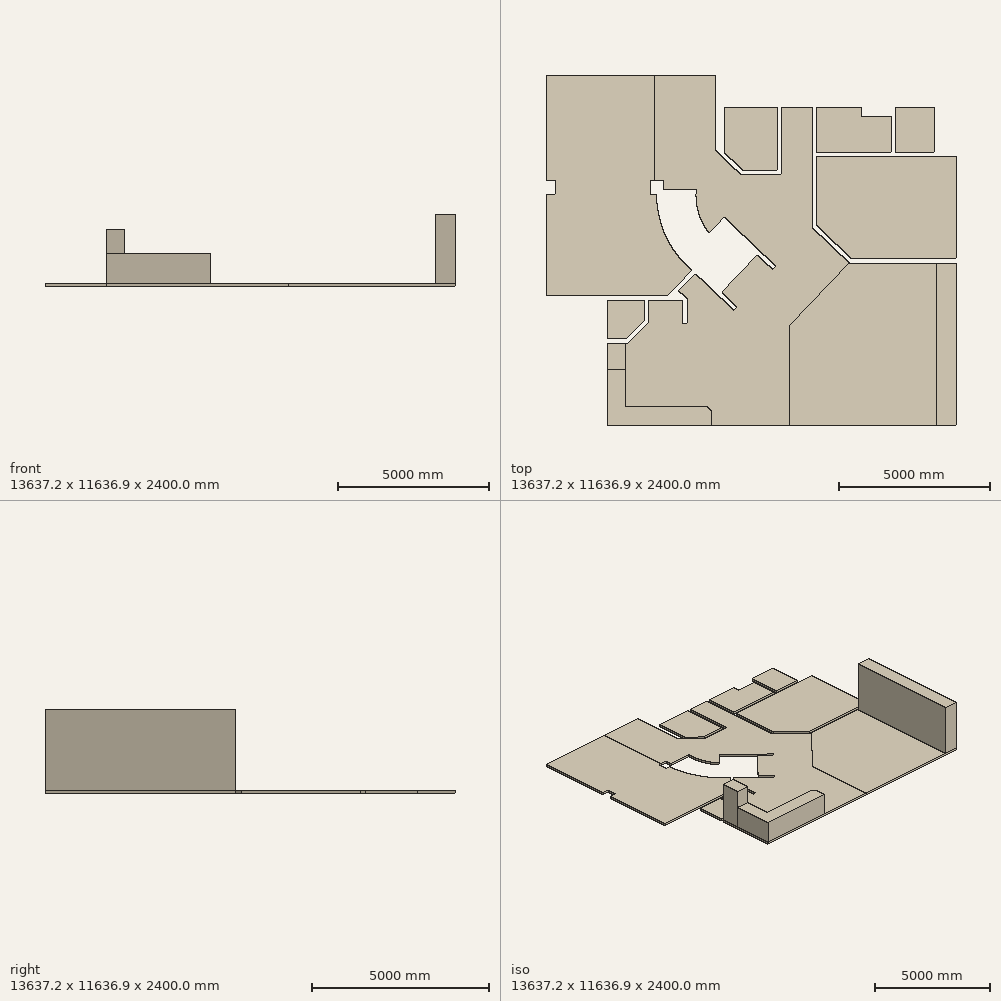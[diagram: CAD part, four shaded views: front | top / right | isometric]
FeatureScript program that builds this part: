
annotation { "Feature Type Name" : "Feature", "Feature Type Description" : "" }
export const myFeature = defineFeature(function(context is Context, id is Id, definition is map)
    precondition{}
    {
        {
            var Q0;
            Q0=qCreatedBy(makeId("Top.planeOp"),FACE);
            var sketch = newSketch(context, id + "F0", { "sketchPlane" : qUnion([Q0])});
            skLineSegment(sketch, "E0", {"start": v(-2600, 0) * mm, "end": v(0, 0) * mm});
            skLineSegment(sketch, "E1", {"start": v(0, 0) * mm, "end": v(0, 3300) * mm});
            skLineSegment(sketch, "E2", {"start": v(770, 6571.43) * mm, "end": v(770, 10720) * mm});
            skLineSegment(sketch, "E3", {"start": v(770, 10720) * mm, "end": v(-230, 10720) * mm});
            skLineSegment(sketch, "E4", {"start": v(-250, 10570) * mm, "end": v(-250, 8330) * mm});
            skLineSegment(sketch, "E5", {"start": v(-250, 8330) * mm, "end": v(-1600, 8330) * mm});
            skLineSegment(sketch, "E6", {"start": v(-1600, 8330) * mm, "end": v(-2447.24, 9136.9) * mm});
            skLineSegment(sketch, "E7", {"start": v(-2447.24, 9136.9) * mm, "end": v(-2447.24, 11636.9) * mm});
            skLineSegment(sketch, "E8", {"start": v(-2447.24, 11636.9) * mm, "end": v(-4497.24, 11636.9) * mm});
            skLineSegment(sketch, "E9", {"start": v(-4497.24, 11636.9) * mm, "end": v(-4497.24, 8136.9) * mm});
            skLineSegment(sketch, "E10", {"start": v(-4497.24, 8136.9) * mm, "end": v(-4197.24, 8136.9) * mm});
            skLineSegment(sketch, "E11", {"start": v(-4197.24, 8136.9) * mm, "end": v(-4197.24, 7836.9) * mm});
            skLineSegment(sketch, "E12", {"start": v(-4197.24, 7836.9) * mm, "end": v(-3097.24, 7836.9) * mm});
            skLineSegment(sketch, "E13", {"start": v(-4830, 3450) * mm, "end": v(-4830, 4170) * mm});
            skLineSegment(sketch, "E14", {"start": v(-4830, 4170) * mm, "end": v(-5900, 4170) * mm});
            skLineSegment(sketch, "E15", {"start": v(-2600, 0) * mm, "end": v(-2600, 488.01) * mm});
            skLineSegment(sketch, "E16", {"start": v(-2600, 488.01) * mm, "end": v(-2730, 640) * mm});
            skLineSegment(sketch, "E17", {"start": v(-2730, 640) * mm, "end": v(-5450, 640) * mm});
            skLineSegment(sketch, "E18", {"start": v(-5450, 640) * mm, "end": v(-5450, 2730) * mm});
            skLineSegment(sketch, "E19", {"start": v(-5400, 2880) * mm, "end": v(-4830, 3450) * mm});
            skLineSegment(sketch, "E20", {"start": v(-4680, 4170) * mm, "end": v(-4680, 3400) * mm});
            skLineSegment(sketch, "E21", {"start": v(-4921.42, 3358.58) * mm, "end": v(-4821.42, 3258.58) * mm});
            skLineSegment(sketch, "E22", {"start": v(-4680, 4170) * mm, "end": v(-3540, 4170) * mm});
            skLineSegment(sketch, "E23", {"start": v(-3540, 4170) * mm, "end": v(-3540, 3400) * mm});
            skLineSegment(sketch, "E24", {"start": v(-3390, 3400) * mm, "end": v(-3540, 3400) * mm});
            skLineSegment(sketch, "E25", {"start": v(-3390, 3400) * mm, "end": v(-3390, 4200) * mm});
            skLineSegment(sketch, "E26", {"start": v(-3125.52, 5049.31) * mm, "end": v(-1843.8, 3828.62) * mm});
            skLineSegment(sketch, "E27", {"start": v(-1843.8, 3828.62) * mm, "end": v(-1740.34, 3937.24) * mm});
            skLineSegment(sketch, "E28", {"start": v(-1740.34, 3937.24) * mm, "end": v(-2247.24, 4420) * mm});
            skLineSegment(sketch, "E29", {"start": v(-2247.24, 4420) * mm, "end": v(-1058.97, 5667.69) * mm});
            skLineSegment(sketch, "E30", {"start": v(-1058.97, 5667.69) * mm, "end": v(-552.07, 5184.93) * mm});
            skLineSegment(sketch, "E31", {"start": v(-552.07, 5184.93) * mm, "end": v(-448.62, 5293.55) * mm});
            skLineSegment(sketch, "E32", {"start": v(-448.62, 5293.55) * mm, "end": v(-2157.59, 6921.14) * mm});
            skLineSegment(sketch, "E33", {"start": v(-2157.59, 6921.14) * mm, "end": v(-2663.1, 6390.34) * mm});
            skArc(sketch, "E34", {"start": v(-3097.24, 7836.9) * mm, "mid": v(-3021.97, 7071.07) * mm, "end": v(-2663.1, 6390.34) * mm});
            skLineSegment(sketch, "E35", {"start": v(0, 0) * mm, "end": v(4900, 0) * mm});
            skLineSegment(sketch, "E36", {"start": v(4900, 0) * mm, "end": v(4900, 5400) * mm});
            skLineSegment(sketch, "E37", {"start": v(4900, 5400) * mm, "end": v(2000, 5400) * mm});
            skLineSegment(sketch, "E38", {"start": v(0, 3300) * mm, "end": v(2000, 5400) * mm});
            skPoint(sketch, "E39", {"position": v(-2450, 0) * mm});
            skLineSegment(sketch, "E40", {"start": v(-2600, 0) * mm, "end": v(-6060, 0) * mm});
            skLineSegment(sketch, "E41", {"start": v(-6060, 0) * mm, "end": v(-6060, 4170) * mm});
            skLineSegment(sketch, "E42", {"start": v(-6060, 4170) * mm, "end": v(-5900, 4170) * mm});
            skLineSegment(sketch, "E43", {"start": v(2000, 5400) * mm, "end": v(770, 6571.43) * mm});
            skLineSegment(sketch, "E44", {"start": v(4900, 0) * mm, "end": v(5560, 0) * mm});
            skLineSegment(sketch, "E45", {"start": v(5560, 0) * mm, "end": v(5560, 10720) * mm});
            skLineSegment(sketch, "E46", {"start": v(5560, 10720) * mm, "end": v(770, 10720) * mm});
            skLineSegment(sketch, "E47", {"start": v(4900, 5400) * mm, "end": v(5560, 5400) * mm});
            skLineSegment(sketch, "E48.0", {"start": v(5810, -250) * mm, "end": v(5810, 10500) * mm});
            skLineSegment(sketch, "E48.1", {"start": v(4900, -250) * mm, "end": v(5810, -250) * mm});
            skLineSegment(sketch, "E48.2", {"start": v(-6310, -250) * mm, "end": v(-6310, 4070) * mm});
            skLineSegment(sketch, "E48.3", {"start": v(-2600, -250) * mm, "end": v(-6310, -250) * mm});
            skLineSegment(sketch, "E48.4", {"start": v(-2600, -250) * mm, "end": v(0, -250) * mm});
            skLineSegment(sketch, "E48.5", {"start": v(0, -250) * mm, "end": v(4900, -250) * mm});
            skLineSegment(sketch, "E49", {"start": v(920, 8930) * mm, "end": v(5560, 8930) * mm});
            skLineSegment(sketch, "E50", {"start": v(920, 9080) * mm, "end": v(5560, 9080) * mm});
            skLineSegment(sketch, "E51", {"start": v(5560, 9080) * mm, "end": v(3540, 9080) * mm});
            skLineSegment(sketch, "E52", {"start": v(3540, 9080) * mm, "end": v(3540, 10570) * mm});
            skLineSegment(sketch, "E53", {"start": v(3390, 9080) * mm, "end": v(3390, 10570) * mm});
            skLineSegment(sketch, "E54.0", {"start": v(5560, 10570) * mm, "end": v(920, 10570) * mm});
            skLineSegment(sketch, "E54.1", {"start": v(4900, 5550) * mm, "end": v(5560, 5550) * mm});
            skLineSegment(sketch, "E54.2", {"start": v(4900, 5550) * mm, "end": v(2060, 5550) * mm});
            skLineSegment(sketch, "E54.3", {"start": v(2060, 5550) * mm, "end": v(920, 6635.71) * mm});
            skLineSegment(sketch, "E54.4", {"start": v(920, 6635.71) * mm, "end": v(920, 10570) * mm});
            skLineSegment(sketch, "E55", {"start": v(3390, 10270) * mm, "end": v(2410, 10270) * mm});
            skLineSegment(sketch, "E56", {"start": v(2410, 10270) * mm, "end": v(2410, 10570) * mm});
            skLineSegment(sketch, "E57", {"start": v(4840, 10570) * mm, "end": v(4840, 9080) * mm});
            skLineSegment(sketch, "E58", {"start": v(920, 10570) * mm, "end": v(-2150, 10570) * mm});
            skLineSegment(sketch, "E59", {"start": v(-2150, 10570) * mm, "end": v(-2150, 9060.95) * mm});
            skLineSegment(sketch, "E60", {"start": v(-2150, 9060.95) * mm, "end": v(-1529.5, 8470) * mm});
            skLineSegment(sketch, "E61", {"start": v(-1529.5, 8470) * mm, "end": v(-400, 8470) * mm});
            skLineSegment(sketch, "E62", {"start": v(-400, 8470) * mm, "end": v(-400, 10570) * mm});
            skLineSegment(sketch, "E63", {"start": v(-6060, 1850) * mm, "end": v(-5450, 1850) * mm});
            skLineSegment(sketch, "E64", {"start": v(-6060, 2730) * mm, "end": v(-5450, 2730) * mm});
            skLineSegment(sketch, "E65", {"start": v(-5450, 2730) * mm, "end": v(-5350, 2730) * mm});
            skLineSegment(sketch, "E66", {"start": v(-5350, 2730) * mm, "end": v(-4680, 3400) * mm});
            skLineSegment(sketch, "E67", {"start": v(-6060, 2880) * mm, "end": v(-5400, 2880) * mm});
            skLineSegment(sketch, "E68", {"start": v(-4027.24, 4320) * mm, "end": v(-8077.24, 4320) * mm});
            skLineSegment(sketch, "E69", {"start": v(-8077.24, 4320) * mm, "end": v(-8077.24, 7696.9) * mm});
            skLineSegment(sketch, "E70", {"start": v(-8077.24, 7696.9) * mm, "end": v(-7767.24, 7696.9) * mm});
            skLineSegment(sketch, "E71", {"start": v(-7767.24, 7696.9) * mm, "end": v(-7767.24, 8136.9) * mm});
            skLineSegment(sketch, "E72", {"start": v(-7767.24, 8136.9) * mm, "end": v(-8077.24, 8136.9) * mm});
            skLineSegment(sketch, "E73", {"start": v(-8077.24, 8136.9) * mm, "end": v(-8077.24, 11636.9) * mm});
            skLineSegment(sketch, "E74", {"start": v(-8077.24, 11636.9) * mm, "end": v(-4497.24, 11636.9) * mm});
            skLineSegment(sketch, "E75", {"start": v(-4497.24, 8136.9) * mm, "end": v(-4627.24, 8136.9) * mm});
            skLineSegment(sketch, "E76", {"start": v(-4627.24, 8136.9) * mm, "end": v(-4627.24, 7696.9) * mm});
            skLineSegment(sketch, "E77", {"start": v(-4627.24, 7696.9) * mm, "end": v(-4417.24, 7696.9) * mm});
            skLineSegment(sketch, "E78", {"start": v(-4027.24, 4320) * mm, "end": v(-3234.14, 5152.76) * mm});
            skArc(sketch, "E79", {"start": v(-4417.24, 7696.9) * mm, "mid": v(-4109.54, 6292.83) * mm, "end": v(-3234.14, 5152.76) * mm});
            skLineSegment(sketch, "E80", {"start": v(-8077.24, 8136.9) * mm, "end": v(-8077.24, 7696.9) * mm});
            skLineSegment(sketch, "E81", {"start": v(-6060, 4320) * mm, "end": v(-6060, 4170) * mm});
            skLineSegment(sketch, "E82.0", {"start": v(-8327.24, 8136.9) * mm, "end": v(-8327.24, 11636.9) * mm});
            skLineSegment(sketch, "E82.1", {"start": v(-8327.24, 8136.9) * mm, "end": v(-8327.24, 7696.9) * mm});
            skLineSegment(sketch, "E82.2", {"start": v(-8327.24, 4320) * mm, "end": v(-8327.24, 7696.9) * mm});
            skLineSegment(sketch, "E83", {"start": v(-6310, 4070) * mm, "end": v(-8327.24, 4070) * mm});
            skLineSegment(sketch, "E84", {"start": v(-8327.24, 4070) * mm, "end": v(-8327.24, 4320) * mm});
            skLineSegment(sketch, "E85", {"start": v(-3125.52, 5049.31) * mm, "end": v(-3675.46, 4471.87) * mm});
            skLineSegment(sketch, "E86", {"start": v(-3675.46, 4471.87) * mm, "end": v(-3390, 4200) * mm});
            skSolve(sketch);
        }
        {
            var Q0;
            Q0=makeQuery(id+"F0.imprint","IMPRINT",FACE,{"disambiguationData":[TD([[makeQuery(id+"F0.imprint","IMPRINT",EDGE,{"derivedFrom":sQuery(id+"F0.wireOp",EDGE,"E0")}),1.0]])]});
            var Q1;
            {var subQ1=sQuery(id+"F0.wireOp",EDGE,"E13");Q1=makeQuery(id+"F0.imprint","IMPRINT",FACE,{"disambiguationData":[TD([[makeQuery(id+"F0.imprint","IMPRINT",EDGE,{"derivedFrom":subQ1}),1.0]])]});}
            var Q2;
            {var subQ0=sQuery(id+"F0.wireOp",EDGE,"fVAch35g-gjPc-Np5k-Pc2o-VTuFZA5Z8obK");Q2=makeQuery(id+"F0.imprint","IMPRINT",FACE,{"disambiguationData":[TD([[makeQuery(id+"F0.imprint","IMPRINT",EDGE,{"derivedFrom":subQ0}),1.0]])]});}
            extrude(context, id + "F1", {"entities" : qUnion([Q0, Q1, Q2]), "oppositeDirection" : true, "depth" : 100 * mm});
        }
        {
            var Q0;
            Q0=makeQuery(id+"F0.imprint","IMPRINT",FACE,{"disambiguationData":[TD([[makeQuery(id+"F0.imprint","IMPRINT",EDGE,{"derivedFrom":sQuery(id+"F0.wireOp",EDGE,"E1")}),-1.0]])]});
            var Q1;
            Q1=makeQuery(id+"F0.imprint","IMPRINT",FACE,{"disambiguationData":[TD([[makeQuery(id+"F0.imprint","IMPRINT",EDGE,{"derivedFrom":sQuery(id+"F0.wireOp",EDGE,"E36")}),-1.0]])]});
            extrude(context, id + "F2", {"entities" : qUnion([Q0, Q1]), "oppositeDirection" : true, "depth" : 100 * mm});
        }
        {
            var Q0;
            Q0=makeQuery(id+"F0.imprint","IMPRINT",FACE,{"disambiguationData":[TD([[makeQuery(id+"F0.imprint","IMPRINT",EDGE,{"derivedFrom":sQuery(id+"F0.wireOp",EDGE,"E9")}),-1.0]])]});
            extrude(context, id + "F3", {"entities" : qUnion([Q0]), "oppositeDirection" : true, "depth" : 100 * mm});
        }
        {
            var Q0;
            {var subQ0=sQuery(id+"F0.wireOp",EDGE,"E59");Q0=makeQuery(id+"F0.imprint","IMPRINT",FACE,{"disambiguationData":[TD([[makeQuery(id+"F0.imprint","IMPRINT",EDGE,{"derivedFrom":subQ0}),1.0]])]});}
            extrude(context, id + "F4", {"entities" : qUnion([Q0]), "oppositeDirection" : true, "depth" : 100 * mm});
        }
        {
            var Q0;
            {var subQ1=sQuery(id+"F0.wireOp",EDGE,"E49");Q0=makeQuery(id+"F0.imprint","IMPRINT",FACE,{"disambiguationData":[TD([[makeQuery(id+"F0.imprint","IMPRINT",EDGE,{"derivedFrom":subQ1}),-1.0]])]});}
            extrude(context, id + "F5", {"entities" : qUnion([Q0]), "oppositeDirection" : true, "depth" : 100 * mm});
        }
        {
            var Q0;
            {var subQ0=sQuery(id+"F0.wireOp",EDGE,"E52");Q0=makeQuery(id+"F0.imprint","IMPRINT",FACE,{"disambiguationData":[TD([[makeQuery(id+"F0.imprint","IMPRINT",EDGE,{"derivedFrom":subQ0}),-1.0]])]});}
            extrude(context, id + "F6", {"entities" : qUnion([Q0]), "oppositeDirection" : true, "depth" : 100 * mm});
        }
        {
            var Q0;
            {var subQ8=sQuery(id+"F0.wireOp",EDGE,"E55");Q0=makeQuery(id+"F0.imprint","IMPRINT",FACE,{"disambiguationData":[TD([[makeQuery(id+"F0.imprint","IMPRINT",EDGE,{"derivedFrom":subQ8}),1.0]])]});}
            extrude(context, id + "F7", {"entities" : qUnion([Q0]), "oppositeDirection" : true, "depth" : 100 * mm});
        }
        {
            var Q0;
            Q0=makeQuery(id+"F0.imprint","IMPRINT",FACE,{"disambiguationData":[TD([[makeQuery(id+"F0.imprint","IMPRINT",EDGE,{"derivedFrom":sQuery(id+"F0.wireOp",EDGE,"E15")}),1.0]])]});
            var Q1;
            {var subQ2=sQuery(id+"F0.wireOp",EDGE,"E63");Q1=makeQuery(id+"F0.imprint","IMPRINT",FACE,{"disambiguationData":[TD([[makeQuery(id+"F0.imprint","IMPRINT",EDGE,{"derivedFrom":subQ2}),1.0]])]});}
            extrude(context, id + "F8", {"entities" : qUnion([Q0, Q1]), "operationType" : NewBodyOperationType.ADD, "oppositeDirection" : true, "depth" : 100 * mm});
        }
        {
            var Q0;
            Q0=makeQuery(id+"F0.imprint","IMPRINT",FACE,{"disambiguationData":[TD([[makeQuery(id+"F0.imprint","IMPRINT",EDGE,{"derivedFrom":sQuery(id+"F0.wireOp",EDGE,"E15")}),1.0]])]});
            extrude(context, id + "F9", {"entities" : qUnion([Q0]), "depth" : 1000 * mm});
        }
        {
            var Q0;
            {var subQ2=sQuery(id+"F0.wireOp",EDGE,"E63");Q0=makeQuery(id+"F0.imprint","IMPRINT",FACE,{"disambiguationData":[TD([[makeQuery(id+"F0.imprint","IMPRINT",EDGE,{"derivedFrom":subQ2}),1.0]])]});}
            extrude(context, id + "F10", {"entities" : qUnion([Q0]), "depth" : 1800 * mm});
        }
        {
            var Q0;
            Q0=makeQuery(id+"F0.imprint","IMPRINT",FACE,{"disambiguationData":[TD([[makeQuery(id+"F0.imprint","IMPRINT",EDGE,{"derivedFrom":sQuery(id+"F0.wireOp",EDGE,"E36")}),-1.0]])]});
            extrude(context, id + "F11", {"entities" : qUnion([Q0]), "depth" : 2300 * mm});
        }
    });
